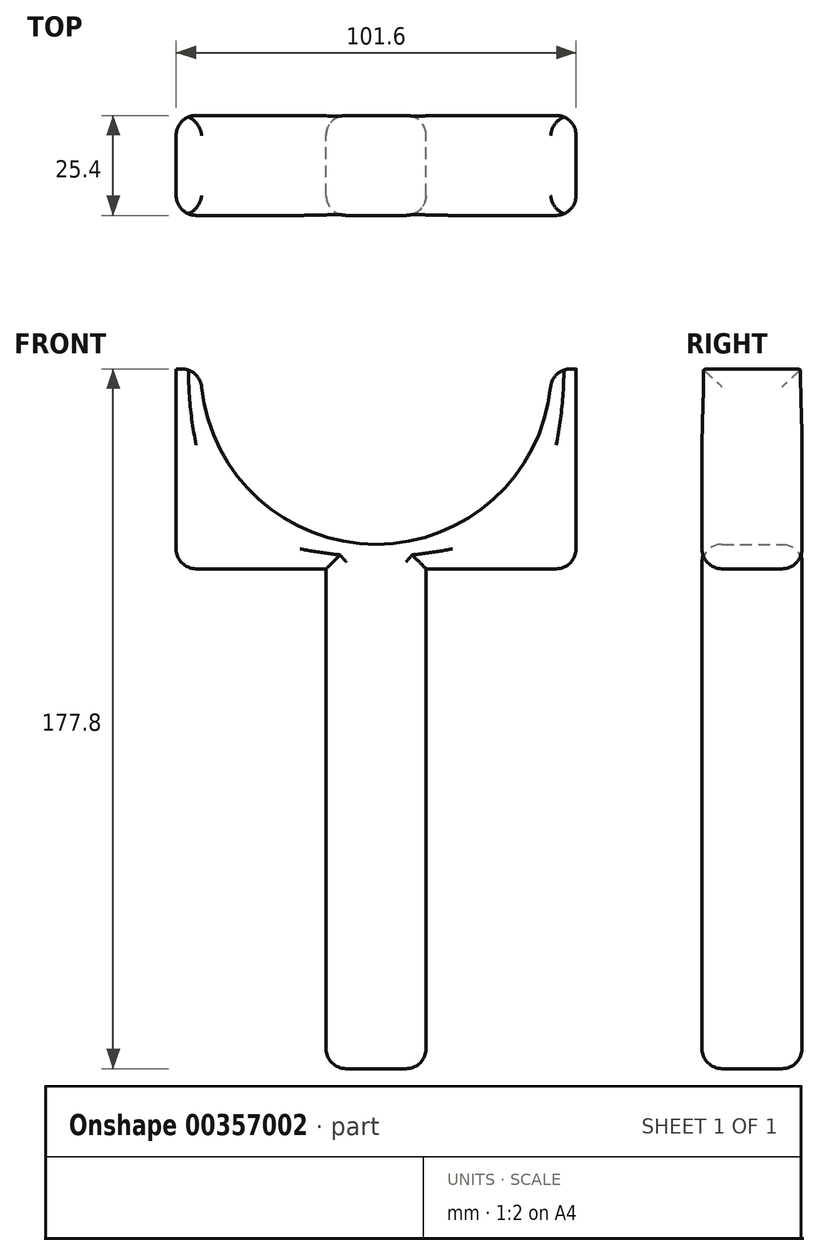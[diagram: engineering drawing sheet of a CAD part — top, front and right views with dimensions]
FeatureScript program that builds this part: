
annotation { "Feature Type Name" : "Feature", "Feature Type Description" : "" }
export const myFeature = defineFeature(function(context is Context, id is Id, definition is map)
    precondition{}
    {
        {
            var Q0;
            Q0=qCreatedBy(makeId("Front.planeOp"),FACE);
            var sketch = newSketch(context, id + "F0", { "sketchPlane" : qUnion([Q0])});
            skLineSegment(sketch, "E0.bottom", {"start": v(12.7, 76.2) * mm, "end": v(-12.7, 76.2) * mm});
            skLineSegment(sketch, "E0.top", {"start": v(12.7, -76.2) * mm, "end": v(-12.7, -76.2) * mm});
            skLineSegment(sketch, "E0.left", {"start": v(12.7, 76.2) * mm, "end": v(12.7, -76.2) * mm});
            skLineSegment(sketch, "E0.right", {"start": v(-12.7, 76.2) * mm, "end": v(-12.7, -76.2) * mm});
            skPoint(sketch, "E0.middle", {"position": v(0, 0) * mm});
            skLineSegment(sketch, "E1.bottom", {"start": v(50.8, 50.8) * mm, "end": v(-50.8, 50.8) * mm});
            skLineSegment(sketch, "E1.top", {"start": v(50.8, 101.6) * mm, "end": v(-50.8, 101.6) * mm});
            skLineSegment(sketch, "E1.left", {"start": v(50.8, 50.8) * mm, "end": v(50.8, 101.6) * mm});
            skLineSegment(sketch, "E1.right", {"start": v(-50.8, 50.8) * mm, "end": v(-50.8, 101.6) * mm});
            skPoint(sketch, "E1.middle", {"position": v(0, 76.2) * mm});
            skCircle(sketch, "E2", {"center": v(0, 101.6) * mm, "radius": 44.57 * mm});
            skSolve(sketch);
        }
        {
            var Q0;
            {var subQ0=sQuery(id+"F0.wireOp",EDGE,"E1.right");Q0=makeQuery(id+"F0.imprint","IMPRINT",FACE,{"disambiguationData":[TD([[makeQuery(id+"F0.imprint","IMPRINT",EDGE,{"derivedFrom":subQ0}),-1.0]])]});}
            var Q1;
            {var subQ0=sQuery(id+"F0.wireOp",EDGE,"E1.left");Q1=makeQuery(id+"F0.imprint","IMPRINT",FACE,{"disambiguationData":[TD([[makeQuery(id+"F0.imprint","IMPRINT",EDGE,{"derivedFrom":subQ0}),1.0]])]});}
            var Q2;
            {var subQ0=sQuery(id+"F0.wireOp",EDGE,"E1.bottom");var subQ1=sQuery(id+"F0.wireOp",EDGE,"E0.left");var subQ2=makeQuery(id+"F0.imprint","INTERSECT",VERTEX,{"derivedFrom":[subQ1,subQ0]});Q2=makeQuery(id+"F0.imprint","IMPRINT",FACE,{"disambiguationData":[TD([[makeQuery(id+"F0.imprint","IMPRINT",EDGE,{"disambiguationData":[TD([[subQ2,1.0]])],"derivedFrom":subQ1}),-1.0]])]});}
            var Q3;
            {var subQ0=sQuery(id+"F0.wireOp",EDGE,"E0.top");Q3=makeQuery(id+"F0.imprint","IMPRINT",FACE,{"disambiguationData":[TD([[makeQuery(id+"F0.imprint","IMPRINT",EDGE,{"derivedFrom":subQ0}),-1.0]])]});}
            extrude(context, id + "F1", {"entities" : qUnion([Q0, Q1, Q2, Q3]), "depth" : 25.4 * mm});
        }
        {
            var Q0;
            Q0=makeQuery(id+"F1.opExtrude","CAP_EDGE",EDGE,{"disambiguationData":[OSD([sQuery(id+"F0.wireOp",EDGE,"E1.right")])],"isStart":false});
            var Q1;
            Q1=makeQuery(id+"F1.opExtrude","CAP_EDGE",EDGE,{"disambiguationData":[OSD([sQuery(id+"F0.wireOp",EDGE,"E1.right")])],"isStart":true});
            var Q2;
            {var subQ0=sQuery(id+"F0.wireOp",EDGE,"E1.bottom");Q2=makeQuery(id+"F1.opExtrude","CAP_EDGE",EDGE,{"disambiguationData":[OSD([subQ0]),TDD([makeQuery(id+"F0.imprint","IMPRINT",EDGE,{"disambiguationData":[TD([[makeQuery(id+"F0.imprint","INTERSECT",VERTEX,{"derivedFrom":[subQ0,sQuery(id+"F0.wireOp",EDGE,"E1.right")]}),1.0]])],"derivedFrom":subQ0})])],"isStart":false});}
            var Q3;
            {var subQ0=sQuery(id+"F0.wireOp",EDGE,"E1.bottom");Q3=makeQuery(id+"F1.opExtrude","CAP_EDGE",EDGE,{"disambiguationData":[OSD([subQ0]),TDD([makeQuery(id+"F0.imprint","IMPRINT",EDGE,{"disambiguationData":[TD([[makeQuery(id+"F0.imprint","INTERSECT",VERTEX,{"derivedFrom":[subQ0,sQuery(id+"F0.wireOp",EDGE,"E1.left")]}),-1.0]])],"derivedFrom":subQ0})])],"isStart":false});}
            var Q4;
            Q4=makeQuery(id+"F1.opExtrude","CAP_EDGE",EDGE,{"disambiguationData":[OSD([sQuery(id+"F0.wireOp",EDGE,"E0.left")])],"isStart":false});
            var Q5;
            Q5=makeQuery(id+"F1.opExtrude","CAP_EDGE",EDGE,{"disambiguationData":[OSD([sQuery(id+"F0.wireOp",EDGE,"E0.right")])],"isStart":false});
            var Q6;
            Q6=makeQuery(id+"F1.opExtrude","CAP_EDGE",EDGE,{"disambiguationData":[OSD([sQuery(id+"F0.wireOp",EDGE,"E0.right")])],"isStart":true});
            var Q7;
            Q7=makeQuery(id+"F1.opExtrude","CAP_EDGE",EDGE,{"disambiguationData":[OSD([sQuery(id+"F0.wireOp",EDGE,"E0.left")])],"isStart":true});
            var Q8;
            {var subQ0=sQuery(id+"F0.wireOp",EDGE,"E1.bottom");Q8=makeQuery(id+"F1.opExtrude","CAP_EDGE",EDGE,{"disambiguationData":[OSD([subQ0]),TDD([makeQuery(id+"F0.imprint","IMPRINT",EDGE,{"disambiguationData":[TD([[makeQuery(id+"F0.imprint","INTERSECT",VERTEX,{"derivedFrom":[subQ0,sQuery(id+"F0.wireOp",EDGE,"E1.right")]}),1.0]])],"derivedFrom":subQ0})])],"isStart":true});}
            var Q9;
            {var subQ0=sQuery(id+"F0.wireOp",EDGE,"E2");var subQ1=sQuery(id+"F0.wireOp",EDGE,"E1.top");Q9=makeQuery(id+"F1.opExtrude","SWEPT_EDGE",EDGE,{"disambiguationData":[OSD([subQ1,subQ0]),TDD([makeQuery(id+"F0.imprint","INTERSECT",VERTEX,{"disambiguationData":[OD(1.0)],"derivedFrom":[subQ1,subQ0]})])]});}
            var Q10;
            Q10=makeQuery(id+"F1.opExtrude","CAP_EDGE",EDGE,{"disambiguationData":[OSD([sQuery(id+"F0.wireOp",EDGE,"E2")])],"isStart":false});
            var Q11;
            Q11=makeQuery(id+"F1.opExtrude","CAP_EDGE",EDGE,{"disambiguationData":[OSD([sQuery(id+"F0.wireOp",EDGE,"E2")])],"isStart":true});
            var Q12;
            Q12=makeQuery(id+"F1.opExtrude","SWEPT_EDGE",EDGE,{"disambiguationData":[OSD([sQuery(id+"F0.wireOp",EDGE,"E1.bottom"),sQuery(id+"F0.wireOp",EDGE,"E1.left")])]});
            var Q13;
            Q13=makeQuery(id+"F1.opExtrude","CAP_EDGE",EDGE,{"disambiguationData":[OSD([sQuery(id+"F0.wireOp",EDGE,"E1.left")])],"isStart":true});
            var Q14;
            Q14=makeQuery(id+"F1.opExtrude","CAP_EDGE",EDGE,{"disambiguationData":[OSD([sQuery(id+"F0.wireOp",EDGE,"E1.left")])],"isStart":false});
            var Q15;
            {var subQ0=sQuery(id+"F0.wireOp",EDGE,"E1.bottom");Q15=makeQuery(id+"F1.opExtrude","CAP_EDGE",EDGE,{"disambiguationData":[OSD([subQ0]),TDD([makeQuery(id+"F0.imprint","IMPRINT",EDGE,{"disambiguationData":[TD([[makeQuery(id+"F0.imprint","INTERSECT",VERTEX,{"derivedFrom":[subQ0,sQuery(id+"F0.wireOp",EDGE,"E1.left")]}),-1.0]])],"derivedFrom":subQ0})])],"isStart":true});}
            var Q16;
            Q16=makeQuery(id+"F1.opExtrude","SWEPT_EDGE",EDGE,{"disambiguationData":[OSD([sQuery(id+"F0.wireOp",EDGE,"E1.bottom"),sQuery(id+"F0.wireOp",EDGE,"E1.right")])]});
            var Q17;
            Q17=makeQuery(id+"F1.opExtrude","CAP_EDGE",EDGE,{"disambiguationData":[OSD([sQuery(id+"F0.wireOp",EDGE,"E0.top")])],"isStart":false});
            var Q18;
            Q18=makeQuery(id+"F1.opExtrude","SWEPT_EDGE",EDGE,{"disambiguationData":[OSD([sQuery(id+"F0.wireOp",EDGE,"E0.top"),sQuery(id+"F0.wireOp",EDGE,"E0.right")])]});
            var Q19;
            Q19=makeQuery(id+"F1.opExtrude","SWEPT_FACE",FACE,{"disambiguationData":[OSD([sQuery(id+"F0.wireOp",EDGE,"E0.top")])]});
            fillet(context, id + "F2", {"entities" : qUnion([Q0, Q1, Q2, Q3, Q4, Q5, Q6, Q7, Q8, Q9, Q10, Q11, Q12, Q13, Q14, Q15, Q16, Q17, Q18, Q19]), "radius" : 5.08 * mm, "tangentPropagation" : true, "allowEdgeOverflow" : false});
        }
        {
            var Q0;
            {var subQ0=sQuery(id+"F0.wireOp",EDGE,"E2");var subQ1=sQuery(id+"F0.wireOp",EDGE,"E1.top");Q0=makeQuery(id+"F1.opExtrude","SWEPT_EDGE",EDGE,{"disambiguationData":[OSD([subQ1,subQ0]),TDD([makeQuery(id+"F0.imprint","INTERSECT",VERTEX,{"disambiguationData":[OD(0.0)],"derivedFrom":[subQ1,subQ0]})])]});}
            fillet(context, id + "F3", {"entities" : qUnion([Q0]), "radius" : 5.08 * mm, "tangentPropagation" : true, "allowEdgeOverflow" : false});
        }
    });
